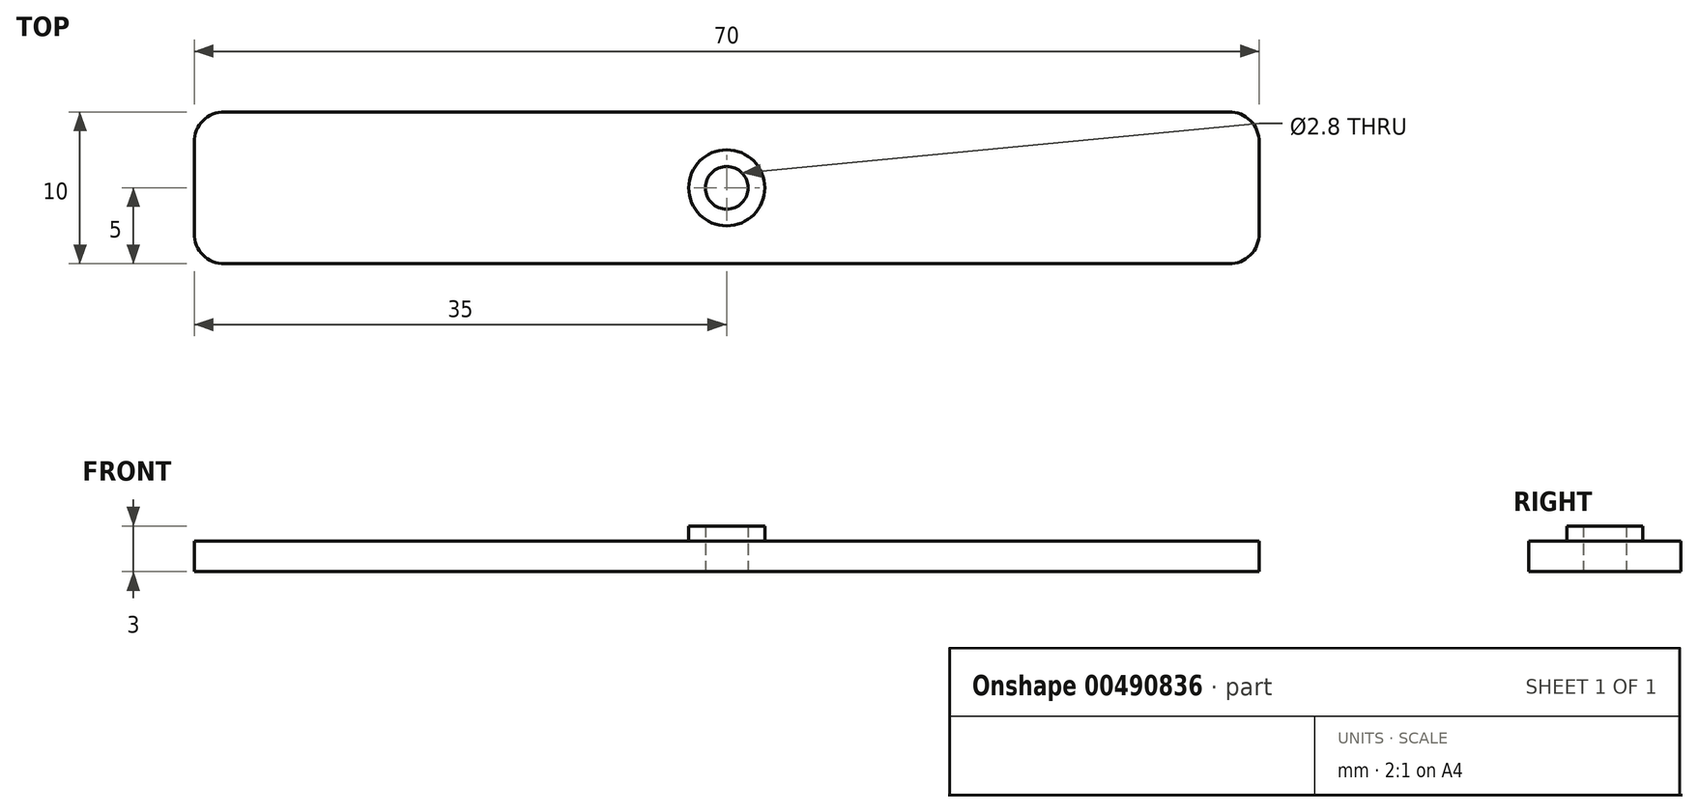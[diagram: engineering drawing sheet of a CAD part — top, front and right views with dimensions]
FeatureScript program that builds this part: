
annotation { "Feature Type Name" : "Feature", "Feature Type Description" : "" }
export const myFeature = defineFeature(function(context is Context, id is Id, definition is map)
    precondition{}
    {
        {
            var Q0;
            Q0=qCreatedBy(makeId("Top.planeOp"),FACE);
            var sketch = newSketch(context, id + "F0", { "sketchPlane" : qUnion([Q0])});
            skLineSegment(sketch, "E0.bottom", {"start": v(35, -5) * mm, "end": v(-35, -5) * mm});
            skLineSegment(sketch, "E0.left", {"start": v(35, -5) * mm, "end": v(35, 5) * mm});
            skLineSegment(sketch, "E0.right", {"start": v(-35, -5) * mm, "end": v(-35, 3.66) * mm});
            skPoint(sketch, "E0.middle", {"position": v(0, 0) * mm});
            skPoint(sketch, "E1.orphan", {"position": v(-35, 5) * mm});
            skPoint(sketch, "E2.start.orphan", {"position": v(0, 5) * mm});
            skPoint(sketch, "E3.MirrorCS.end.orphan", {"position": v(35, 3.66) * mm});
            skLineSegment(sketch, "E4", {"start": v(0, 5) * mm, "end": v(-35, 5) * mm});
            skLineSegment(sketch, "E5", {"start": v(-35, 3.66) * mm, "end": v(-35, 5) * mm});
            skLineSegment(sketch, "E6", {"start": v(0, 5) * mm, "end": v(35, 5) * mm});
            skCircle(sketch, "E7", {"center": v(0, 0) * mm, "radius": 1.4 * mm});
            skCircle(sketch, "E8", {"center": v(0, 0) * mm, "radius": 2.5 * mm});
            skSolve(sketch);
        }
        {
            var Q0;
            Q0=makeQuery(id+"F0.imprint","IMPRINT",FACE,{"disambiguationData":[TD([[makeQuery(id+"F0.imprint","IMPRINT",EDGE,{"derivedFrom":sQuery(id+"F0.wireOp",EDGE,"E0.bottom")}),-1.0]])]});
            extrude(context, id + "F1", {"entities" : qUnion([Q0]), "depth" : 2 * mm, "offsetDistance" : 25 * mm});
        }
        {
            var Q0;
            Q0=makeQuery(id+"F1.opExtrude","SWEPT_EDGE",EDGE,{"disambiguationData":[OSD([sQuery(id+"F0.wireOp",EDGE,"E4"),sQuery(id+"F0.wireOp",EDGE,"E5")])]});
            var Q1;
            Q1=makeQuery(id+"F1.opExtrude","SWEPT_EDGE",EDGE,{"disambiguationData":[OSD([sQuery(id+"F0.wireOp",EDGE,"E0.bottom"),sQuery(id+"F0.wireOp",EDGE,"E0.right")])]});
            var Q2;
            Q2=makeQuery(id+"F1.opExtrude","SWEPT_EDGE",EDGE,{"disambiguationData":[OSD([sQuery(id+"F0.wireOp",EDGE,"E0.bottom"),sQuery(id+"F0.wireOp",EDGE,"E0.left")])]});
            var Q3;
            Q3=makeQuery(id+"F1.opExtrude","SWEPT_EDGE",EDGE,{"disambiguationData":[OSD([sQuery(id+"F0.wireOp",EDGE,"E0.left"),sQuery(id+"F0.wireOp",EDGE,"E6")])]});
            fillet(context, id + "F2", {"entities" : qUnion([Q0, Q1, Q2, Q3]), "radius" : 2 * mm, "tangentPropagation" : true, "allowEdgeOverflow" : false});
        }
        {
            var Q0;
            Q0=makeQuery(id+"F0.imprint","IMPRINT",FACE,{"disambiguationData":[TD([[makeQuery(id+"F0.imprint","IMPRINT",EDGE,{"derivedFrom":sQuery(id+"F0.wireOp",EDGE,"E7")}),-1.0]])]});
            extrude(context, id + "F3", {"entities" : qUnion([Q0]), "operationType" : NewBodyOperationType.ADD, "depth" : 3 * mm, "offsetDistance" : 25 * mm});
        }
    });
